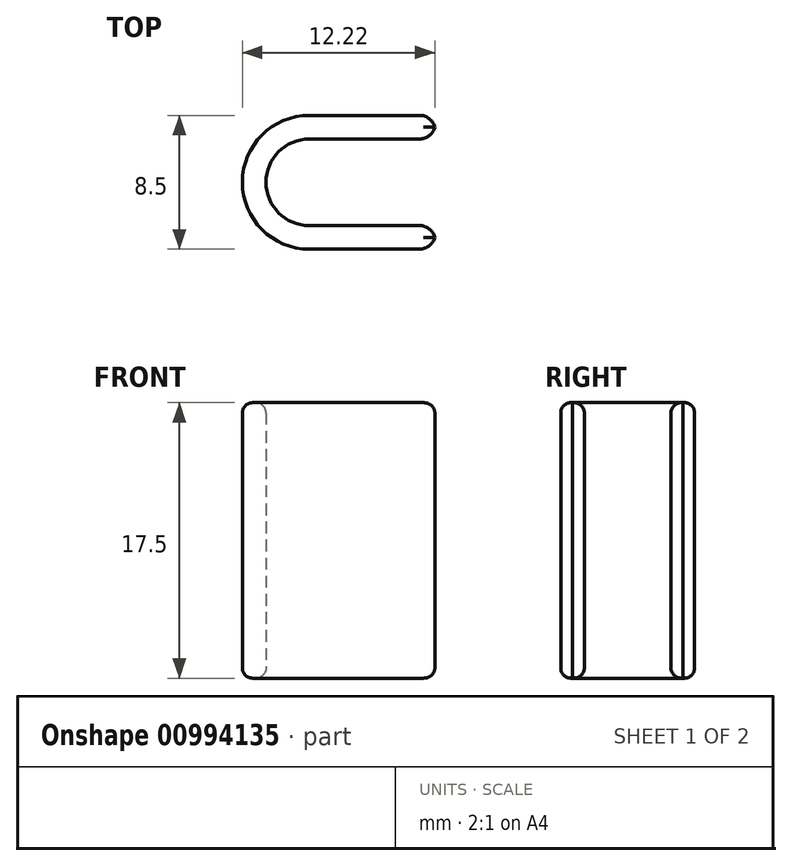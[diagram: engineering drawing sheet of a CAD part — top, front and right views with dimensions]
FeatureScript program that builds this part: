
annotation { "Feature Type Name" : "Feature", "Feature Type Description" : "" }
export const myFeature = defineFeature(function(context is Context, id is Id, definition is map)
    precondition{}
    {
        {
            var Q0;
            Q0=qCreatedBy(makeId("Top.planeOp"),FACE);
            var sketch = newSketch(context, id + "F0", { "sketchPlane" : qUnion([Q0])});
            skArc(sketch, "E0", {"start": v(0, 2.75) * mm, "mid": v(-2.75, 0) * mm, "end": v(0, -2.75) * mm});
            skArc(sketch, "E1", {"start": v(0, 4.25) * mm, "mid": v(-4.25, 0) * mm, "end": v(0, -4.25) * mm});
            skLineSegment(sketch, "E2", {"start": v(0, 2.75) * mm, "end": v(8, 2.75) * mm});
            skLineSegment(sketch, "E3", {"start": v(8, 2.75) * mm, "end": v(8, 4.25) * mm});
            skLineSegment(sketch, "E4", {"start": v(8, 4.25) * mm, "end": v(0, 4.25) * mm});
            skLineSegment(sketch, "E5", {"start": v(0, -2.75) * mm, "end": v(8, -2.75) * mm});
            skLineSegment(sketch, "E6", {"start": v(8, -2.75) * mm, "end": v(8, -4.25) * mm});
            skLineSegment(sketch, "E7", {"start": v(8, -4.25) * mm, "end": v(0, -4.25) * mm});
            skSolve(sketch);
        }
        {
            var Q0;
            Q0=makeQuery(id+"F0.imprint","IMPRINT",FACE,{"disambiguationData":[TD([[makeQuery(id+"F0.imprint","IMPRINT",EDGE,{"derivedFrom":sQuery(id+"F0.wireOp",EDGE,"E0")}),-1.0]])]});
            extrude(context, id + "F1", {"entities" : qUnion([Q0]), "depth" : 17.5 * mm, "offsetDistance" : 25 * mm});
        }
        {
            var Q0;
            Q0=makeQuery(id+"F1.opExtrude","SWEPT_EDGE",EDGE,{"disambiguationData":[OSD([sQuery(id+"F0.wireOp",EDGE,"E5"),sQuery(id+"F0.wireOp",EDGE,"E6")])]});
            var Q1;
            Q1=makeQuery(id+"F1.opExtrude","SWEPT_EDGE",EDGE,{"disambiguationData":[OSD([sQuery(id+"F0.wireOp",EDGE,"E6"),sQuery(id+"F0.wireOp",EDGE,"E7")])]});
            var Q2;
            Q2=makeQuery(id+"F1.opExtrude","SWEPT_EDGE",EDGE,{"disambiguationData":[OSD([sQuery(id+"F0.wireOp",EDGE,"E2"),sQuery(id+"F0.wireOp",EDGE,"E3")])]});
            var Q3;
            Q3=makeQuery(id+"F1.opExtrude","SWEPT_EDGE",EDGE,{"disambiguationData":[OSD([sQuery(id+"F0.wireOp",EDGE,"E3"),sQuery(id+"F0.wireOp",EDGE,"E4")])]});
            fillet(context, id + "F2", {"entities" : qUnion([Q0, Q1, Q2, Q3]), "radius" : 1 * mm, "tangentPropagation" : true, "allowEdgeOverflow" : false});
        }
        {
            var Q0;
            Q0=makeQuery(id+"F1.opExtrude","CAP_FACE",FACE,{"disambiguationData":[OSD([sQuery(id+"F0.wireOp",EDGE,"E0"),sQuery(id+"F0.wireOp",EDGE,"E1"),sQuery(id+"F0.wireOp",EDGE,"E2"),sQuery(id+"F0.wireOp",EDGE,"E3"),sQuery(id+"F0.wireOp",EDGE,"E4"),sQuery(id+"F0.wireOp",EDGE,"E5"),sQuery(id+"F0.wireOp",EDGE,"E6"),sQuery(id+"F0.wireOp",EDGE,"E7")])],"isStart":true});
            var Q1;
            Q1=makeQuery(id+"F1.opExtrude","CAP_FACE",FACE,{"disambiguationData":[OSD([sQuery(id+"F0.wireOp",EDGE,"E0"),sQuery(id+"F0.wireOp",EDGE,"E1"),sQuery(id+"F0.wireOp",EDGE,"E2"),sQuery(id+"F0.wireOp",EDGE,"E3"),sQuery(id+"F0.wireOp",EDGE,"E4"),sQuery(id+"F0.wireOp",EDGE,"E5"),sQuery(id+"F0.wireOp",EDGE,"E6"),sQuery(id+"F0.wireOp",EDGE,"E7")])],"isStart":false});
            fillet(context, id + "F3", {"entities" : qUnion([Q0, Q1]), "radius" : 0.65 * mm, "tangentPropagation" : true, "allowEdgeOverflow" : false});
        }
    });
